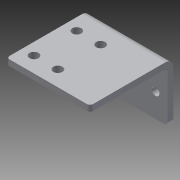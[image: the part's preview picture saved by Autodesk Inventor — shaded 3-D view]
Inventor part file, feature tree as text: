
AUTODESK INVENTOR PART (.ipt)
format: ipt  version: 2014 (Build 180170000, 170)  size: 137,216 bytes
history: native  units: in
note: dims shown in document units (in); Inventor stores cm internally (conversion verified against a paired STEP export)
features: sheet_metal_op x4, sketch x3, other x2, fillet x1, extrude x1
ambient origin geometry x8: Origin, YZ Plane, XZ Plane, XY Plane, X Axis, Y Axis, Z Axis, Center Point
bodies: Solid1 (feature_tree)
feature tree (11):
  sheet_metal_op  "Face1"
  sheet_metal_op  "Flange1"
  fillet  "Fillet1"  Radius=1.75in
  extrude  "Extrusion1"  Depth=0.163in
  sketch  "Sketch1"  dims[d1=1.0in d2=0.163in]
  other  "Plate1"
  sketch  "Sketch2"  dims[d4=0.7874in d6=1.0in d7=0.3937in d9=1.0in]
  other  "Plate2"
  sheet_metal_op  "Bend1"
  sheet_metal_op  "Corner1"
  sketch  "Sketch3"  dims[d11=0.125in d12=0.125in d13=0.0625in d14=0.25in d15=0.125in d16=1.75in d17=90.0deg d18=0.05in d19=0.5in d20=0.125in d21=0.125in d22=0.0625in d23=1.35in d24=0.75in d25=0.125in d27=0.19in d28=0.125in d29=0.2265in d30=1.0in d31=0.0in d32=0.25in d33=0.875in]
